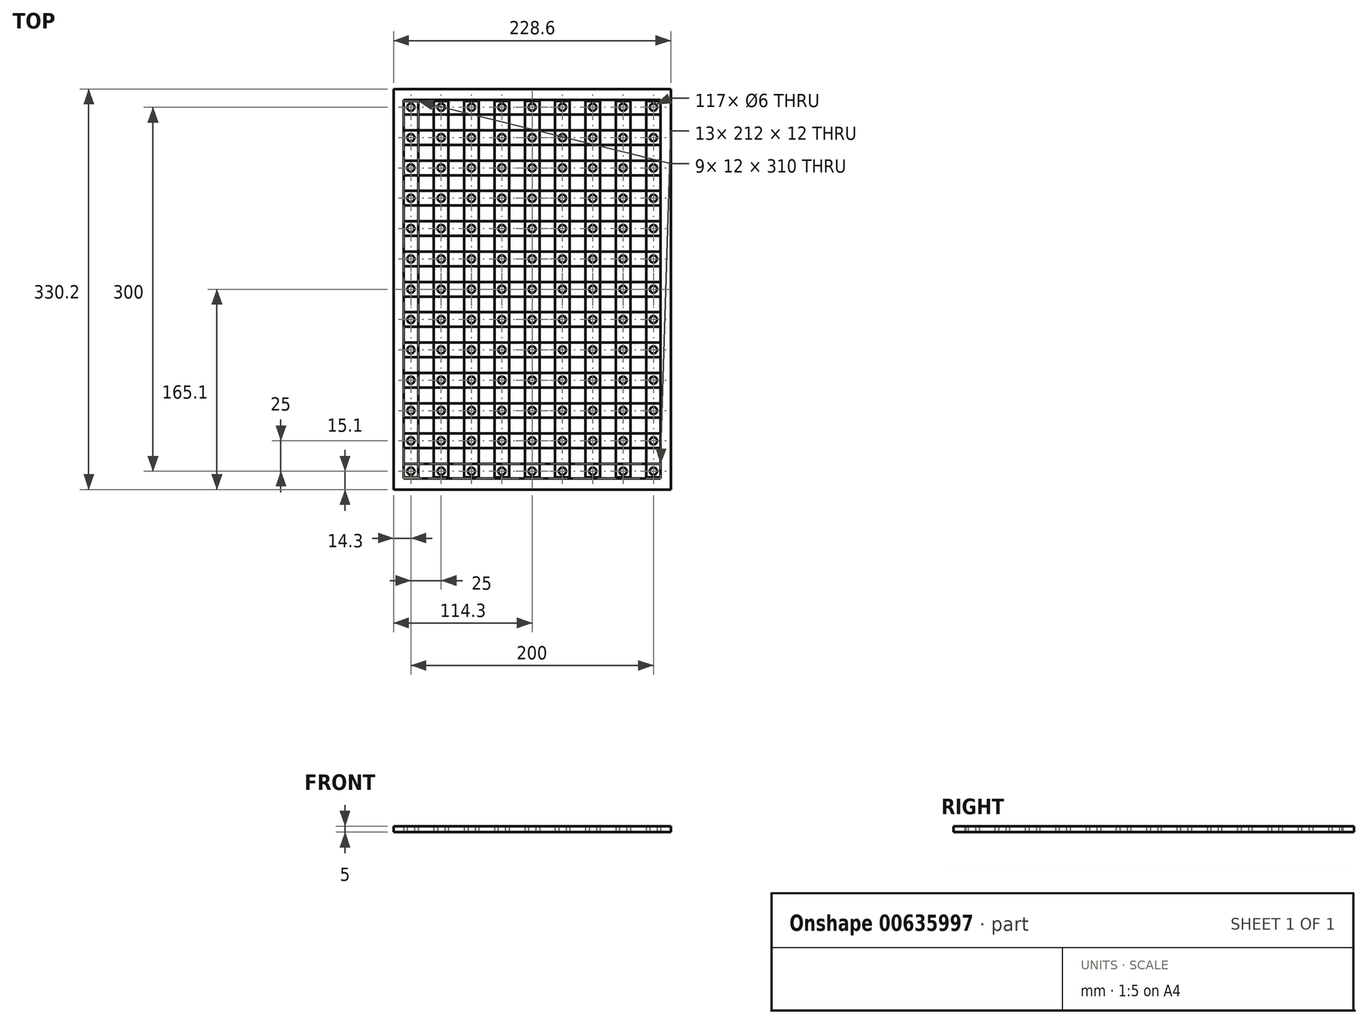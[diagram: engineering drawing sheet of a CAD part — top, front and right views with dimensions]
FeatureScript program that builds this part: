
annotation { "Feature Type Name" : "Feature", "Feature Type Description" : "" }
export const myFeature = defineFeature(function(context is Context, id is Id, definition is map)
    precondition{}
    {
        {
            var Q0;
            Q0=qCreatedBy(makeId("Top.planeOp"),FACE);
            var sketch = newSketch(context, id + "F0", { "sketchPlane" : qUnion([Q0])});
            skLineSegment(sketch, "E0.bottom", {"start": v(114.3, 165.1) * mm, "end": v(-114.3, 165.1) * mm});
            skLineSegment(sketch, "E0.top", {"start": v(114.3, -165.1) * mm, "end": v(-114.3, -165.1) * mm});
            skLineSegment(sketch, "E0.left", {"start": v(114.3, 165.1) * mm, "end": v(114.3, -165.1) * mm});
            skLineSegment(sketch, "E0.right", {"start": v(-114.3, 165.1) * mm, "end": v(-114.3, -165.1) * mm});
            skPoint(sketch, "E0.middle", {"position": v(0, 0) * mm});
            skLineSegment(sketch, "E1.bottom", {"start": v(6, 155) * mm, "end": v(-6, 155) * mm});
            skLineSegment(sketch, "E1.top", {"start": v(6, -155) * mm, "end": v(-6, -155) * mm});
            skLineSegment(sketch, "E1.left", {"start": v(6, 155) * mm, "end": v(6, -155) * mm});
            skLineSegment(sketch, "E1.right", {"start": v(-6, 155) * mm, "end": v(-6, -155) * mm});
            skLineSegment(sketch, "E2.1.0.0", {"start": v(31, 155) * mm, "end": v(19, 155) * mm});
            skLineSegment(sketch, "E2.1.0.1", {"start": v(19, 155) * mm, "end": v(19, -155) * mm});
            skLineSegment(sketch, "E2.1.0.2", {"start": v(31, -155) * mm, "end": v(19, -155) * mm});
            skPoint(sketch, "E2.1.0.3", {"position": v(25, 0) * mm});
            skLineSegment(sketch, "E2.1.0.4", {"start": v(31, 155) * mm, "end": v(31, -155) * mm});
            skPoint(sketch, "E2.1.0.5", {"position": v(25, 0) * mm});
            skLineSegment(sketch, "E2.2.0.0", {"start": v(56, 155) * mm, "end": v(44, 155) * mm});
            skLineSegment(sketch, "E2.2.0.1", {"start": v(44, 155) * mm, "end": v(44, -155) * mm});
            skLineSegment(sketch, "E2.2.0.2", {"start": v(56, -155) * mm, "end": v(44, -155) * mm});
            skPoint(sketch, "E2.2.0.3", {"position": v(50, 0) * mm});
            skLineSegment(sketch, "E2.2.0.4", {"start": v(56, 155) * mm, "end": v(56, -155) * mm});
            skPoint(sketch, "E2.2.0.5", {"position": v(50, 0) * mm});
            skLineSegment(sketch, "E2.3.0.0", {"start": v(81, 155) * mm, "end": v(69, 155) * mm});
            skLineSegment(sketch, "E2.3.0.1", {"start": v(69, 155) * mm, "end": v(69, -155) * mm});
            skLineSegment(sketch, "E2.3.0.2", {"start": v(81, -155) * mm, "end": v(69, -155) * mm});
            skPoint(sketch, "E2.3.0.3", {"position": v(75, 0) * mm});
            skLineSegment(sketch, "E2.3.0.4", {"start": v(81, 155) * mm, "end": v(81, -155) * mm});
            skPoint(sketch, "E2.3.0.5", {"position": v(75, 0) * mm});
            skLineSegment(sketch, "E2.4.0.0", {"start": v(106, 155) * mm, "end": v(94, 155) * mm});
            skLineSegment(sketch, "E2.4.0.1", {"start": v(94, 155) * mm, "end": v(94, -155) * mm});
            skLineSegment(sketch, "E2.4.0.2", {"start": v(106, -155) * mm, "end": v(94, -155) * mm});
            skPoint(sketch, "E2.4.0.3", {"position": v(100, 0) * mm});
            skLineSegment(sketch, "E2.4.0.4", {"start": v(106, 155) * mm, "end": v(106, -155) * mm});
            skPoint(sketch, "E2.4.0.5", {"position": v(100, 0) * mm});
            skLineSegment(sketch, "E2.direction1", {"start": v(-6, -155) * mm, "end": v(19, -155) * mm, "construction": true});
            skLineSegment(sketch, "E3", {"start": v(0, -190.9) * mm, "end": v(0, 194.6) * mm, "construction": true});
            skPoint(sketch, "E3.endSnap0", {"position": v(0, 165.1) * mm});
            skLineSegment(sketch, "E4.MirrorCS", {"start": v(-81, 155) * mm, "end": v(-69, 155) * mm});
            skLineSegment(sketch, "E5.MirrorCS", {"start": v(-56, 155) * mm, "end": v(-44, 155) * mm});
            skLineSegment(sketch, "E6.MirrorCS", {"start": v(-106, -155) * mm, "end": v(-94, -155) * mm});
            skLineSegment(sketch, "E7.MirrorCS", {"start": v(-106, 155) * mm, "end": v(-94, 155) * mm});
            skLineSegment(sketch, "E8.MirrorCS", {"start": v(-56, -155) * mm, "end": v(-44, -155) * mm});
            skLineSegment(sketch, "E9.MirrorCS", {"start": v(-31, -155) * mm, "end": v(-19, -155) * mm});
            skLineSegment(sketch, "E10.MirrorCS", {"start": v(-81, -155) * mm, "end": v(-69, -155) * mm});
            skLineSegment(sketch, "E11.MirrorCS", {"start": v(-31, 155) * mm, "end": v(-19, 155) * mm});
            skPoint(sketch, "E12.MirrorP", {"position": v(-50, 0) * mm});
            skPoint(sketch, "E13.MirrorP", {"position": v(-25, 0) * mm});
            skPoint(sketch, "E14.MirrorP", {"position": v(-100, 0) * mm});
            skPoint(sketch, "E15.MirrorP", {"position": v(-75, 0) * mm});
            skLineSegment(sketch, "E16.MirrorCS", {"start": v(-94, 155) * mm, "end": v(-94, -155) * mm});
            skLineSegment(sketch, "E17.MirrorCS", {"start": v(-31, 155) * mm, "end": v(-31, -155) * mm});
            skLineSegment(sketch, "E18.MirrorCS", {"start": v(-69, 155) * mm, "end": v(-69, -155) * mm});
            skLineSegment(sketch, "E19.MirrorCS", {"start": v(-44, 155) * mm, "end": v(-44, -155) * mm});
            skLineSegment(sketch, "E20.MirrorCS", {"start": v(-106, 155) * mm, "end": v(-106, -155) * mm});
            skLineSegment(sketch, "E21.MirrorCS", {"start": v(-56, 155) * mm, "end": v(-56, -155) * mm});
            skLineSegment(sketch, "E22.MirrorCS", {"start": v(-81, 155) * mm, "end": v(-81, -155) * mm});
            skLineSegment(sketch, "E23.MirrorCS", {"start": v(-19, 155) * mm, "end": v(-19, -155) * mm});
            skSolve(sketch);
        }
        {
            var Q0;
            Q0=makeQuery(id+"F0.imprint","IMPRINT",FACE,{"disambiguationData":[TD([[makeQuery(id+"F0.imprint","IMPRINT",EDGE,{"derivedFrom":sQuery(id+"F0.wireOp",EDGE,"E0.bottom")}),1.0]])]});
            extrude(context, id + "F1", {"entities" : qUnion([Q0]), "depth" : 5 * mm, "offsetDistance" : 25 * mm});
        }
        {
            var Q0;
            Q0=qCreatedBy(makeId("Top.planeOp"),FACE);
            var sketch = newSketch(context, id + "F2", { "sketchPlane" : qUnion([Q0])});
            skPoint(sketch, "E24.0", {"position": v(-114.3, 165.1) * mm});
            skPoint(sketch, "E25.0", {"position": v(114.3, -165.1) * mm});
            skPoint(sketch, "E26.0", {"position": v(106, 0) * mm});
            skPoint(sketch, "E27.0", {"position": v(-106, 0) * mm});
            skPoint(sketch, "E28.0", {"position": v(0, 155) * mm});
            skPoint(sketch, "E29.0", {"position": v(0, -155) * mm});
            skLineSegment(sketch, "E30.bottom", {"start": v(-114.3, 165.1) * mm, "end": v(114.3, 165.1) * mm});
            skLineSegment(sketch, "E30.top", {"start": v(-114.3, -165.1) * mm, "end": v(114.3, -165.1) * mm});
            skLineSegment(sketch, "E30.left", {"start": v(-114.3, 165.1) * mm, "end": v(-114.3, -165.1) * mm});
            skLineSegment(sketch, "E30.right", {"start": v(114.3, 165.1) * mm, "end": v(114.3, -165.1) * mm});
            skLineSegment(sketch, "E31.bottom", {"start": v(106, 6) * mm, "end": v(-106, 6) * mm});
            skLineSegment(sketch, "E31.top", {"start": v(106, -6) * mm, "end": v(-106, -6) * mm});
            skLineSegment(sketch, "E31.left", {"start": v(106, 6) * mm, "end": v(106, -6) * mm});
            skLineSegment(sketch, "E31.right", {"start": v(-106, 6) * mm, "end": v(-106, -6) * mm});
            skPoint(sketch, "E31.middle", {"position": v(0, 0) * mm});
            skLineSegment(sketch, "E32.0.1.0", {"start": v(106, 31) * mm, "end": v(-106, 31) * mm});
            skPoint(sketch, "E32.0.1.1", {"position": v(-106, 25) * mm});
            skPoint(sketch, "E32.0.1.2", {"position": v(106, 25) * mm});
            skPoint(sketch, "E32.0.1.3", {"position": v(0, 25) * mm});
            skLineSegment(sketch, "E32.0.1.4", {"start": v(106, 19) * mm, "end": v(-106, 19) * mm});
            skLineSegment(sketch, "E32.0.1.5", {"start": v(106, 31) * mm, "end": v(106, 19) * mm});
            skLineSegment(sketch, "E32.0.1.6", {"start": v(-106, 31) * mm, "end": v(-106, 19) * mm});
            skLineSegment(sketch, "E32.0.2.0", {"start": v(106, 56) * mm, "end": v(-106, 56) * mm});
            skPoint(sketch, "E32.0.2.1", {"position": v(-106, 50) * mm});
            skPoint(sketch, "E32.0.2.2", {"position": v(106, 50) * mm});
            skPoint(sketch, "E32.0.2.3", {"position": v(0, 50) * mm});
            skLineSegment(sketch, "E32.0.2.4", {"start": v(106, 44) * mm, "end": v(-106, 44) * mm});
            skLineSegment(sketch, "E32.0.2.5", {"start": v(106, 56) * mm, "end": v(106, 44) * mm});
            skLineSegment(sketch, "E32.0.2.6", {"start": v(-106, 56) * mm, "end": v(-106, 44) * mm});
            skLineSegment(sketch, "E32.0.3.0", {"start": v(106, 81) * mm, "end": v(-106, 81) * mm});
            skPoint(sketch, "E32.0.3.1", {"position": v(-106, 75) * mm});
            skPoint(sketch, "E32.0.3.2", {"position": v(106, 75) * mm});
            skPoint(sketch, "E32.0.3.3", {"position": v(0, 75) * mm});
            skLineSegment(sketch, "E32.0.3.4", {"start": v(106, 69) * mm, "end": v(-106, 69) * mm});
            skLineSegment(sketch, "E32.0.3.5", {"start": v(106, 81) * mm, "end": v(106, 69) * mm});
            skLineSegment(sketch, "E32.0.3.6", {"start": v(-106, 81) * mm, "end": v(-106, 69) * mm});
            skLineSegment(sketch, "E32.0.4.0", {"start": v(106, 106) * mm, "end": v(-106, 106) * mm});
            skPoint(sketch, "E32.0.4.1", {"position": v(-106, 100) * mm});
            skPoint(sketch, "E32.0.4.2", {"position": v(106, 100) * mm});
            skPoint(sketch, "E32.0.4.3", {"position": v(0, 100) * mm});
            skLineSegment(sketch, "E32.0.4.4", {"start": v(106, 94) * mm, "end": v(-106, 94) * mm});
            skLineSegment(sketch, "E32.0.4.5", {"start": v(106, 106) * mm, "end": v(106, 94) * mm});
            skLineSegment(sketch, "E32.0.4.6", {"start": v(-106, 106) * mm, "end": v(-106, 94) * mm});
            skLineSegment(sketch, "E32.0.5.0", {"start": v(106, 131) * mm, "end": v(-106, 131) * mm});
            skPoint(sketch, "E32.0.5.1", {"position": v(-106, 125) * mm});
            skPoint(sketch, "E32.0.5.2", {"position": v(106, 125) * mm});
            skPoint(sketch, "E32.0.5.3", {"position": v(0, 125) * mm});
            skLineSegment(sketch, "E32.0.5.4", {"start": v(106, 119) * mm, "end": v(-106, 119) * mm});
            skLineSegment(sketch, "E32.0.5.5", {"start": v(106, 131) * mm, "end": v(106, 119) * mm});
            skLineSegment(sketch, "E32.0.5.6", {"start": v(-106, 131) * mm, "end": v(-106, 119) * mm});
            skLineSegment(sketch, "E32.0.6.0", {"start": v(106, 156) * mm, "end": v(-106, 156) * mm});
            skPoint(sketch, "E32.0.6.1", {"position": v(-106, 150) * mm});
            skPoint(sketch, "E32.0.6.2", {"position": v(106, 150) * mm});
            skPoint(sketch, "E32.0.6.3", {"position": v(0, 150) * mm});
            skLineSegment(sketch, "E32.0.6.4", {"start": v(106, 144) * mm, "end": v(-106, 144) * mm});
            skLineSegment(sketch, "E32.0.6.5", {"start": v(106, 156) * mm, "end": v(106, 144) * mm});
            skLineSegment(sketch, "E32.0.6.6", {"start": v(-106, 156) * mm, "end": v(-106, 144) * mm});
            skLineSegment(sketch, "E32.direction1", {"start": v(-106, -6) * mm, "end": v(-81, -6) * mm, "construction": true});
            skLineSegment(sketch, "E32.direction2", {"start": v(-106, -6) * mm, "end": v(-106, 19) * mm, "construction": true});
            skLineSegment(sketch, "E33", {"start": v(-170.2, 0) * mm, "end": v(191.94, 0) * mm, "construction": true});
            skLineSegment(sketch, "E34.MirrorCS", {"start": v(106, -81) * mm, "end": v(106, -69) * mm});
            skLineSegment(sketch, "E35.MirrorCS", {"start": v(-106, -156) * mm, "end": v(-106, -144) * mm});
            skLineSegment(sketch, "E36.MirrorCS", {"start": v(106, -106) * mm, "end": v(106, -94) * mm});
            skLineSegment(sketch, "E37.MirrorCS", {"start": v(-106, -81) * mm, "end": v(-106, -69) * mm});
            skLineSegment(sketch, "E38.MirrorCS", {"start": v(106, -31) * mm, "end": v(106, -19) * mm});
            skLineSegment(sketch, "E39.MirrorCS", {"start": v(-106, -31) * mm, "end": v(-106, -19) * mm});
            skLineSegment(sketch, "E40.MirrorCS", {"start": v(106, -131) * mm, "end": v(106, -119) * mm});
            skLineSegment(sketch, "E41.MirrorCS", {"start": v(106, -156) * mm, "end": v(106, -144) * mm});
            skLineSegment(sketch, "E42.MirrorCS", {"start": v(-106, -106) * mm, "end": v(-106, -94) * mm});
            skLineSegment(sketch, "E43.MirrorCS", {"start": v(-106, -131) * mm, "end": v(-106, -119) * mm});
            skLineSegment(sketch, "E44.MirrorCS", {"start": v(-106, -56) * mm, "end": v(-106, -44) * mm});
            skLineSegment(sketch, "E45.MirrorCS", {"start": v(106, -56) * mm, "end": v(106, -44) * mm});
            skPoint(sketch, "E46.MirrorP", {"position": v(0, -100) * mm});
            skLineSegment(sketch, "E47.MirrorCS", {"start": v(-106, 6) * mm, "end": v(-106, -19) * mm, "construction": true});
            skPoint(sketch, "E48.MirrorP", {"position": v(106, -125) * mm});
            skPoint(sketch, "E49.MirrorP", {"position": v(0, -75) * mm});
            skLineSegment(sketch, "E50.MirrorCS", {"start": v(106, -31) * mm, "end": v(-106, -31) * mm});
            skLineSegment(sketch, "E51.MirrorCS", {"start": v(106, -19) * mm, "end": v(-106, -19) * mm});
            skLineSegment(sketch, "E52.MirrorCS", {"start": v(106, -144) * mm, "end": v(-106, -144) * mm});
            skLineSegment(sketch, "E53.MirrorCS", {"start": v(106, -81) * mm, "end": v(-106, -81) * mm});
            skLineSegment(sketch, "E54.MirrorCS", {"start": v(106, -119) * mm, "end": v(-106, -119) * mm});
            skPoint(sketch, "E55.MirrorP", {"position": v(106, -150) * mm});
            skPoint(sketch, "E56.MirrorP", {"position": v(-106, -150) * mm});
            skPoint(sketch, "E57.MirrorP", {"position": v(0, -50) * mm});
            skLineSegment(sketch, "E58.MirrorCS", {"start": v(106, -56) * mm, "end": v(-106, -56) * mm});
            skPoint(sketch, "E59.MirrorP", {"position": v(106, -100) * mm});
            skPoint(sketch, "E60.MirrorP", {"position": v(106, -25) * mm});
            skPoint(sketch, "E61.MirrorP", {"position": v(-106, -50) * mm});
            skPoint(sketch, "E62.MirrorP", {"position": v(-114.3, -165.1) * mm});
            skLineSegment(sketch, "E63.MirrorCS", {"start": v(106, -131) * mm, "end": v(-106, -131) * mm});
            skLineSegment(sketch, "E64.MirrorCS", {"start": v(106, -156) * mm, "end": v(-106, -156) * mm});
            skLineSegment(sketch, "E65.MirrorCS", {"start": v(106, -69) * mm, "end": v(-106, -69) * mm});
            skLineSegment(sketch, "E66.MirrorCS", {"start": v(106, -94) * mm, "end": v(-106, -94) * mm});
            skPoint(sketch, "E67.MirrorP", {"position": v(0, -150) * mm});
            skPoint(sketch, "E68.MirrorP", {"position": v(106, -75) * mm});
            skPoint(sketch, "E69.MirrorP", {"position": v(106, -50) * mm});
            skLineSegment(sketch, "E70.MirrorCS", {"start": v(106, -106) * mm, "end": v(-106, -106) * mm});
            skPoint(sketch, "E71.MirrorP", {"position": v(-106, -100) * mm});
            skPoint(sketch, "E72.MirrorP", {"position": v(-106, -75) * mm});
            skLineSegment(sketch, "E73.MirrorCS", {"start": v(106, -44) * mm, "end": v(-106, -44) * mm});
            skPoint(sketch, "E74.MirrorP", {"position": v(-106, -25) * mm});
            skPoint(sketch, "E75.MirrorP", {"position": v(-106, -125) * mm});
            skPoint(sketch, "E76.MirrorP", {"position": v(0, -125) * mm});
            skPoint(sketch, "E77.MirrorP", {"position": v(0, -25) * mm});
            skSolve(sketch);
        }
        {
            var Q0;
            Q0=makeQuery(id+"F2.imprint","IMPRINT",FACE,{"disambiguationData":[TD([[makeQuery(id+"F2.imprint","IMPRINT",EDGE,{"derivedFrom":sQuery(id+"F2.wireOp",EDGE,"E30.bottom")}),-1.0]])]});
            extrude(context, id + "F3", {"entities" : qUnion([Q0]), "depth" : 5 * mm, "offsetDistance" : 25 * mm});
        }
        {
            var Q0;
            Q0=qCreatedBy(makeId("Top.planeOp"),FACE);
            var sketch = newSketch(context, id + "F4", { "sketchPlane" : qUnion([Q0])});
            skCircle(sketch, "E78", {"center": v(0, 0) * mm, "radius": 3 * mm});
            skCircle(sketch, "E79.0.1.0", {"center": v(0, 25) * mm, "radius": 3 * mm});
            skCircle(sketch, "E79.0.2.0", {"center": v(0, 50) * mm, "radius": 3 * mm});
            skCircle(sketch, "E79.0.3.0", {"center": v(0, 75) * mm, "radius": 3 * mm});
            skCircle(sketch, "E79.0.4.0", {"center": v(0, 100) * mm, "radius": 3 * mm});
            skCircle(sketch, "E79.0.5.0", {"center": v(0, 125) * mm, "radius": 3 * mm});
            skCircle(sketch, "E79.0.6.0", {"center": v(0, 150) * mm, "radius": 3 * mm});
            skCircle(sketch, "E79.1.0.0", {"center": v(25, 0) * mm, "radius": 3 * mm});
            skCircle(sketch, "E79.1.1.0", {"center": v(25, 25) * mm, "radius": 3 * mm});
            skCircle(sketch, "E79.1.2.0", {"center": v(25, 50) * mm, "radius": 3 * mm});
            skCircle(sketch, "E79.1.3.0", {"center": v(25, 75) * mm, "radius": 3 * mm});
            skCircle(sketch, "E79.1.4.0", {"center": v(25, 100) * mm, "radius": 3 * mm});
            skCircle(sketch, "E79.1.5.0", {"center": v(25, 125) * mm, "radius": 3 * mm});
            skCircle(sketch, "E79.1.6.0", {"center": v(25, 150) * mm, "radius": 3 * mm});
            skCircle(sketch, "E79.2.0.0", {"center": v(50, 0) * mm, "radius": 3 * mm});
            skCircle(sketch, "E79.2.1.0", {"center": v(50, 25) * mm, "radius": 3 * mm});
            skCircle(sketch, "E79.2.2.0", {"center": v(50, 50) * mm, "radius": 3 * mm});
            skCircle(sketch, "E79.2.3.0", {"center": v(50, 75) * mm, "radius": 3 * mm});
            skCircle(sketch, "E79.2.4.0", {"center": v(50, 100) * mm, "radius": 3 * mm});
            skCircle(sketch, "E79.2.5.0", {"center": v(50, 125) * mm, "radius": 3 * mm});
            skCircle(sketch, "E79.2.6.0", {"center": v(50, 150) * mm, "radius": 3 * mm});
            skCircle(sketch, "E79.3.0.0", {"center": v(75, 0) * mm, "radius": 3 * mm});
            skCircle(sketch, "E79.3.1.0", {"center": v(75, 25) * mm, "radius": 3 * mm});
            skCircle(sketch, "E79.3.2.0", {"center": v(75, 50) * mm, "radius": 3 * mm});
            skCircle(sketch, "E79.3.3.0", {"center": v(75, 75) * mm, "radius": 3 * mm});
            skCircle(sketch, "E79.3.4.0", {"center": v(75, 100) * mm, "radius": 3 * mm});
            skCircle(sketch, "E79.3.5.0", {"center": v(75, 125) * mm, "radius": 3 * mm});
            skCircle(sketch, "E79.3.6.0", {"center": v(75, 150) * mm, "radius": 3 * mm});
            skCircle(sketch, "E79.4.0.0", {"center": v(100, 0) * mm, "radius": 3 * mm});
            skCircle(sketch, "E79.4.1.0", {"center": v(100, 25) * mm, "radius": 3 * mm});
            skCircle(sketch, "E79.4.2.0", {"center": v(100, 50) * mm, "radius": 3 * mm});
            skCircle(sketch, "E79.4.3.0", {"center": v(100, 75) * mm, "radius": 3 * mm});
            skCircle(sketch, "E79.4.4.0", {"center": v(100, 100) * mm, "radius": 3 * mm});
            skCircle(sketch, "E79.4.5.0", {"center": v(100, 125) * mm, "radius": 3 * mm});
            skCircle(sketch, "E79.4.6.0", {"center": v(100, 150) * mm, "radius": 3 * mm});
            skLineSegment(sketch, "E79.direction1", {"start": v(0, 0) * mm, "end": v(25, 0) * mm, "construction": true});
            skLineSegment(sketch, "E79.direction2", {"start": v(0, 0) * mm, "end": v(0, 25) * mm, "construction": true});
            skLineSegment(sketch, "E80", {"start": v(-143.7, 0) * mm, "end": v(184.82, 0) * mm, "construction": true});
            skLineSegment(sketch, "E81", {"start": v(184.82, 0) * mm, "end": v(184.82, -2.77) * mm, "construction": true});
            skLineSegment(sketch, "E82", {"start": v(0, -169.2) * mm, "end": v(0, 171.97) * mm, "construction": true});
            skCircle(sketch, "E83.MirrorC", {"center": v(0, -25) * mm, "radius": 3 * mm});
            skCircle(sketch, "E84.MirrorC", {"center": v(50, -50) * mm, "radius": 3 * mm});
            skCircle(sketch, "E85.MirrorC", {"center": v(100, -50) * mm, "radius": 3 * mm});
            skCircle(sketch, "E86.MirrorC", {"center": v(25, -25) * mm, "radius": 3 * mm});
            skCircle(sketch, "E87.MirrorC", {"center": v(50, -100) * mm, "radius": 3 * mm});
            skCircle(sketch, "E88.MirrorC", {"center": v(0, -100) * mm, "radius": 3 * mm});
            skCircle(sketch, "E89.MirrorC", {"center": v(50, -25) * mm, "radius": 3 * mm});
            skCircle(sketch, "E90.MirrorC", {"center": v(100, -75) * mm, "radius": 3 * mm});
            skCircle(sketch, "E91.MirrorC", {"center": v(0, -50) * mm, "radius": 3 * mm});
            skCircle(sketch, "E92.MirrorC", {"center": v(25, -75) * mm, "radius": 3 * mm});
            skCircle(sketch, "E93.MirrorC", {"center": v(75, -25) * mm, "radius": 3 * mm});
            skCircle(sketch, "E94.MirrorC", {"center": v(25, -100) * mm, "radius": 3 * mm});
            skCircle(sketch, "E95.MirrorC", {"center": v(75, -75) * mm, "radius": 3 * mm});
            skCircle(sketch, "E96.MirrorC", {"center": v(75, -100) * mm, "radius": 3 * mm});
            skCircle(sketch, "E97.MirrorC", {"center": v(50, -125) * mm, "radius": 3 * mm});
            skCircle(sketch, "E98.MirrorC", {"center": v(25, -125) * mm, "radius": 3 * mm});
            skCircle(sketch, "E99.MirrorC", {"center": v(75, -125) * mm, "radius": 3 * mm});
            skCircle(sketch, "E100.MirrorC", {"center": v(75, -50) * mm, "radius": 3 * mm});
            skCircle(sketch, "E101.MirrorC", {"center": v(100, -25) * mm, "radius": 3 * mm});
            skCircle(sketch, "E102.MirrorC", {"center": v(100, -100) * mm, "radius": 3 * mm});
            skCircle(sketch, "E103.MirrorC", {"center": v(0, -75) * mm, "radius": 3 * mm});
            skCircle(sketch, "E104.MirrorC", {"center": v(25, -150) * mm, "radius": 3 * mm});
            skCircle(sketch, "E105.MirrorC", {"center": v(0, -125) * mm, "radius": 3 * mm});
            skCircle(sketch, "E106.MirrorC", {"center": v(0, -150) * mm, "radius": 3 * mm});
            skCircle(sketch, "E107.MirrorC", {"center": v(50, -150) * mm, "radius": 3 * mm});
            skCircle(sketch, "E108.MirrorC", {"center": v(75, -150) * mm, "radius": 3 * mm});
            skCircle(sketch, "E109.MirrorC", {"center": v(100, -125) * mm, "radius": 3 * mm});
            skCircle(sketch, "E110.MirrorC", {"center": v(25, -50) * mm, "radius": 3 * mm});
            skCircle(sketch, "E111.MirrorC", {"center": v(50, -75) * mm, "radius": 3 * mm});
            skLineSegment(sketch, "E112.MirrorCS", {"start": v(0, 0) * mm, "end": v(0, -25) * mm, "construction": true});
            skCircle(sketch, "E113.MirrorC", {"center": v(100, -150) * mm, "radius": 3 * mm});
            skLineSegment(sketch, "E114.MirrorCS", {"start": v(0, 169.2) * mm, "end": v(0, -171.97) * mm, "construction": true});
            skCircle(sketch, "E115.MirrorC", {"center": v(-25, 0) * mm, "radius": 3 * mm});
            skCircle(sketch, "E116.MirrorC", {"center": v(-100, -150) * mm, "radius": 3 * mm});
            skCircle(sketch, "E117.MirrorC", {"center": v(-50, 50) * mm, "radius": 3 * mm});
            skCircle(sketch, "E118.MirrorC", {"center": v(-100, 100) * mm, "radius": 3 * mm});
            skCircle(sketch, "E119.MirrorC", {"center": v(-75, -100) * mm, "radius": 3 * mm});
            skCircle(sketch, "E120.MirrorC", {"center": v(-100, 25) * mm, "radius": 3 * mm});
            skCircle(sketch, "E121.MirrorC", {"center": v(-75, 25) * mm, "radius": 3 * mm});
            skCircle(sketch, "E122.MirrorC", {"center": v(-25, -25) * mm, "radius": 3 * mm});
            skCircle(sketch, "E123.MirrorC", {"center": v(-75, -25) * mm, "radius": 3 * mm});
            skCircle(sketch, "E124.MirrorC", {"center": v(-100, -100) * mm, "radius": 3 * mm});
            skCircle(sketch, "E125.MirrorC", {"center": v(-100, -125) * mm, "radius": 3 * mm});
            skCircle(sketch, "E126.MirrorC", {"center": v(-25, 150) * mm, "radius": 3 * mm});
            skCircle(sketch, "E127.MirrorC", {"center": v(-50, 150) * mm, "radius": 3 * mm});
            skCircle(sketch, "E128.MirrorC", {"center": v(-50, -50) * mm, "radius": 3 * mm});
            skCircle(sketch, "E129.MirrorC", {"center": v(-75, -50) * mm, "radius": 3 * mm});
            skCircle(sketch, "E130.MirrorC", {"center": v(-75, 100) * mm, "radius": 3 * mm});
            skCircle(sketch, "E131.MirrorC", {"center": v(-50, -25) * mm, "radius": 3 * mm});
            skCircle(sketch, "E132.MirrorC", {"center": v(-25, 50) * mm, "radius": 3 * mm});
            skCircle(sketch, "E133.MirrorC", {"center": v(-50, -75) * mm, "radius": 3 * mm});
            skCircle(sketch, "E134.MirrorC", {"center": v(-50, 25) * mm, "radius": 3 * mm});
            skCircle(sketch, "E135.MirrorC", {"center": v(-100, 75) * mm, "radius": 3 * mm});
            skCircle(sketch, "E136.MirrorC", {"center": v(-75, -75) * mm, "radius": 3 * mm});
            skCircle(sketch, "E137.MirrorC", {"center": v(-100, 0) * mm, "radius": 3 * mm});
            skCircle(sketch, "E138.MirrorC", {"center": v(-75, 75) * mm, "radius": 3 * mm});
            skCircle(sketch, "E139.MirrorC", {"center": v(-25, -75) * mm, "radius": 3 * mm});
            skCircle(sketch, "E140.MirrorC", {"center": v(-75, -150) * mm, "radius": 3 * mm});
            skCircle(sketch, "E141.MirrorC", {"center": v(-25, -150) * mm, "radius": 3 * mm});
            skCircle(sketch, "E142.MirrorC", {"center": v(-25, 125) * mm, "radius": 3 * mm});
            skCircle(sketch, "E143.MirrorC", {"center": v(-50, 125) * mm, "radius": 3 * mm});
            skCircle(sketch, "E144.MirrorC", {"center": v(-75, -125) * mm, "radius": 3 * mm});
            skCircle(sketch, "E145.MirrorC", {"center": v(-25, 100) * mm, "radius": 3 * mm});
            skCircle(sketch, "E146.MirrorC", {"center": v(-75, 125) * mm, "radius": 3 * mm});
            skCircle(sketch, "E147.MirrorC", {"center": v(-100, -75) * mm, "radius": 3 * mm});
            skCircle(sketch, "E148.MirrorC", {"center": v(-25, 75) * mm, "radius": 3 * mm});
            skCircle(sketch, "E149.MirrorC", {"center": v(-50, 100) * mm, "radius": 3 * mm});
            skCircle(sketch, "E150.MirrorC", {"center": v(-50, -100) * mm, "radius": 3 * mm});
            skCircle(sketch, "E151.MirrorC", {"center": v(-100, 50) * mm, "radius": 3 * mm});
            skCircle(sketch, "E152.MirrorC", {"center": v(-50, 0) * mm, "radius": 3 * mm});
            skCircle(sketch, "E153.MirrorC", {"center": v(-50, 75) * mm, "radius": 3 * mm});
            skCircle(sketch, "E154.MirrorC", {"center": v(-50, -125) * mm, "radius": 3 * mm});
            skCircle(sketch, "E155.MirrorC", {"center": v(-25, -100) * mm, "radius": 3 * mm});
            skCircle(sketch, "E156.MirrorC", {"center": v(-75, 50) * mm, "radius": 3 * mm});
            skCircle(sketch, "E157.MirrorC", {"center": v(-100, -25) * mm, "radius": 3 * mm});
            skCircle(sketch, "E158.MirrorC", {"center": v(-75, 0) * mm, "radius": 3 * mm});
            skCircle(sketch, "E159.MirrorC", {"center": v(-25, -125) * mm, "radius": 3 * mm});
            skCircle(sketch, "E160.MirrorC", {"center": v(-25, -50) * mm, "radius": 3 * mm});
            skCircle(sketch, "E161.MirrorC", {"center": v(-100, 150) * mm, "radius": 3 * mm});
            skCircle(sketch, "E162.MirrorC", {"center": v(-100, -50) * mm, "radius": 3 * mm});
            skCircle(sketch, "E163.MirrorC", {"center": v(-100, 125) * mm, "radius": 3 * mm});
            skCircle(sketch, "E164.MirrorC", {"center": v(-50, -150) * mm, "radius": 3 * mm});
            skCircle(sketch, "E165.MirrorC", {"center": v(-75, 150) * mm, "radius": 3 * mm});
            skLineSegment(sketch, "E166.MirrorCS", {"start": v(0, 0) * mm, "end": v(-25, 0) * mm, "construction": true});
            skCircle(sketch, "E167.MirrorC", {"center": v(-25, 25) * mm, "radius": 3 * mm});
            skLineSegment(sketch, "E168.MirrorCS", {"start": v(143.7, 0) * mm, "end": v(-184.82, 0) * mm, "construction": true});
            skPoint(sketch, "E169.0", {"position": v(-114.3, 165.1) * mm});
            skPoint(sketch, "E170.0", {"position": v(114.3, -165.1) * mm});
            skLineSegment(sketch, "E171.bottom", {"start": v(-114.3, 165.1) * mm, "end": v(114.3, 165.1) * mm});
            skLineSegment(sketch, "E171.top", {"start": v(-114.3, -165.1) * mm, "end": v(114.3, -165.1) * mm});
            skLineSegment(sketch, "E171.left", {"start": v(-114.3, 165.1) * mm, "end": v(-114.3, -165.1) * mm});
            skLineSegment(sketch, "E171.right", {"start": v(114.3, 165.1) * mm, "end": v(114.3, -165.1) * mm});
            skSolve(sketch);
        }
        {
            var Q0;
            Q0=makeQuery(id+"F4.imprint","IMPRINT",FACE,{"disambiguationData":[TD([[makeQuery(id+"F4.imprint","IMPRINT",EDGE,{"derivedFrom":sQuery(id+"F4.wireOp",EDGE,"E78")}),-1.0]])]});
            extrude(context, id + "F5", {"entities" : qUnion([Q0]), "depth" : 5 * mm, "offsetDistance" : 25 * mm});
        }
        {
            var Q0;
            Q0=qCreatedBy(makeId("Top.planeOp"),FACE);
            var sketch = newSketch(context, id + "F6", { "sketchPlane" : qUnion([Q0])});
            skPoint(sketch, "E172.0", {"position": v(-114.3, 165.1) * mm});
            skPoint(sketch, "E173.0", {"position": v(114.3, -165.1) * mm});
            skLineSegment(sketch, "E174.bottom", {"start": v(-114.3, 165.1) * mm, "end": v(114.3, 165.1) * mm});
            skLineSegment(sketch, "E174.top", {"start": v(-114.3, -165.1) * mm, "end": v(114.3, -165.1) * mm});
            skLineSegment(sketch, "E174.left", {"start": v(-114.3, 165.1) * mm, "end": v(-114.3, -165.1) * mm});
            skLineSegment(sketch, "E174.right", {"start": v(114.3, 165.1) * mm, "end": v(114.3, -165.1) * mm});
            skSolve(sketch);
        }
        {
            var Q0;
            Q0=makeQuery(id+"F6.imprint","IMPRINT",FACE,{"disambiguationData":[TD([[makeQuery(id+"F6.imprint","IMPRINT",EDGE,{"derivedFrom":sQuery(id+"F6.wireOp",EDGE,"E174.bottom")}),-1.0]])]});
            extrude(context, id + "F7", {"entities" : qUnion([Q0]), "depth" : 5 * mm, "offsetDistance" : 25 * mm});
        }
    });
